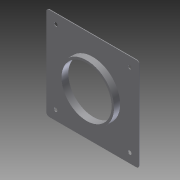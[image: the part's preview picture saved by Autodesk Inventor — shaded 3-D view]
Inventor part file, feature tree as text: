
AUTODESK INVENTOR PART (.ipt)
format: ipt  version: 2011 (Build 150239000, 239)  size: 150,528 bytes
history: native  units: in
note: dims shown in document units (in); Inventor stores cm internally (conversion verified against a paired STEP export)
features: extrude x10, sketch x10, fillet x1
ambient origin geometry x8: Origin, YZ Plane, XZ Plane, XY Plane, X Axis, Y Axis, Z Axis, Center Point
bodies: Solid1 (feature_tree)
feature tree (21):
  extrude  "Extrusion1"  Depth=4.0in
  extrude  "Extrusion2"  Depth=2.16in
  extrude  "Extrusion3"  Depth=1.7655in
  extrude  "Extrusion4"  Depth=0.029in TaperAngle=0.0deg
  extrude  "Extrusion5"  Depth=2.36in
  fillet  "Fillet1"  Radius=2.56in
  extrude  "Extrusion6"  Depth=0.125in
  extrude  "Extrusion7"  Depth=0.262in TaperAngle=0.0deg
  extrude  "Extrusion8"  Depth=0.029in TaperAngle=0.0deg
  extrude  "Extrusion9"  Depth=0.156in
  extrude  "Extrusion10"  [1 undecoded]
  sketch  "Sketch1"  dims[d0=4.0in d1=4.0in]
  sketch  "Sketch2"  dims[d2=0.029in d3=0.0in d4=2.16in]
  sketch  "Sketch3"  dims[d5=0.029in d6=0.0in d7=1.7655in]
  sketch  "Sketch4"  dims[d8=0.156in d9=0.029in d10=0.0in]
  sketch  "Sketch5"  dims[d11=0.029in d12=0.0in d13=2.36in d14=2.56in]
  sketch  "Sketch6"  dims[d15=0.262in d16=0.0in d17=0.125in]
  sketch  "Sketch7"  dims[d18=0.362in d19=0.0in d20=0.262in d21=0.0in]
  sketch  "Sketch8"  dims[d22=0.1in d23=0.0in d24=0.029in d25=0.0in]
  sketch  "Sketch9"  dims[d26=1.594in d27=0.156in]
  sketch  "Sketch10"  dims[d28=0.029in d29=0.0in]
note: 1 required parameter value undecoded (feature->parameter linkage not recoverable at this tier; creation-order binding heuristic only, values carry confidence <= 0.55)
